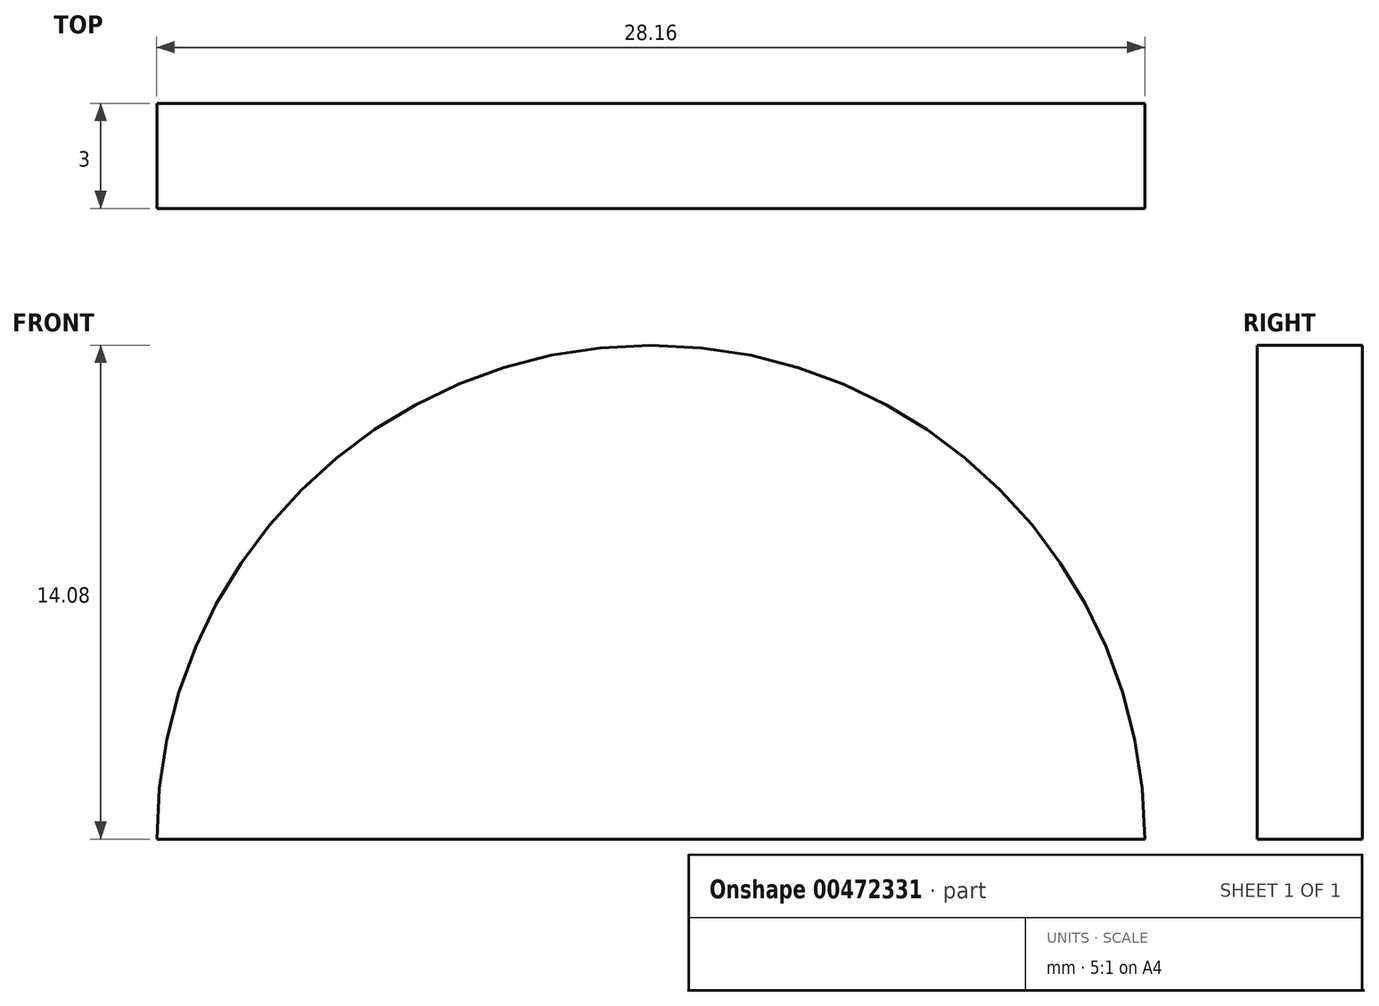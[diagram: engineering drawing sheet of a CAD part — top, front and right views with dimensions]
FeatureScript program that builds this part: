
annotation { "Feature Type Name" : "Feature", "Feature Type Description" : "" }
export const myFeature = defineFeature(function(context is Context, id is Id, definition is map)
    precondition{}
    {
        {
            var Q0;
            Q0=qCreatedBy(makeId("Front.planeOp"),FACE);
            var sketch = newSketch(context, id + "F0", { "sketchPlane" : qUnion([Q0])});
            skLineSegment(sketch, "E0", {"start": v(-14.42, 0) * mm, "end": v(14.08, 0) * mm});
            skLineSegment(sketch, "E1", {"start": v(14.08, 0) * mm, "end": v(-14.42, 0) * mm});
            skArc(sketch, "E2", {"start": v(14.08, 0) * mm, "mid": v(0, 14.08) * mm, "end": v(-14.08, 0) * mm});
            skSolve(sketch);
        }
        {
            var Q0;
            Q0 = qSketchRegion(id + "F0", true);
            extrude(context, id + "F1", {"entities" : qUnion([Q0]), "depth" : 3 * mm});
        }
    });
